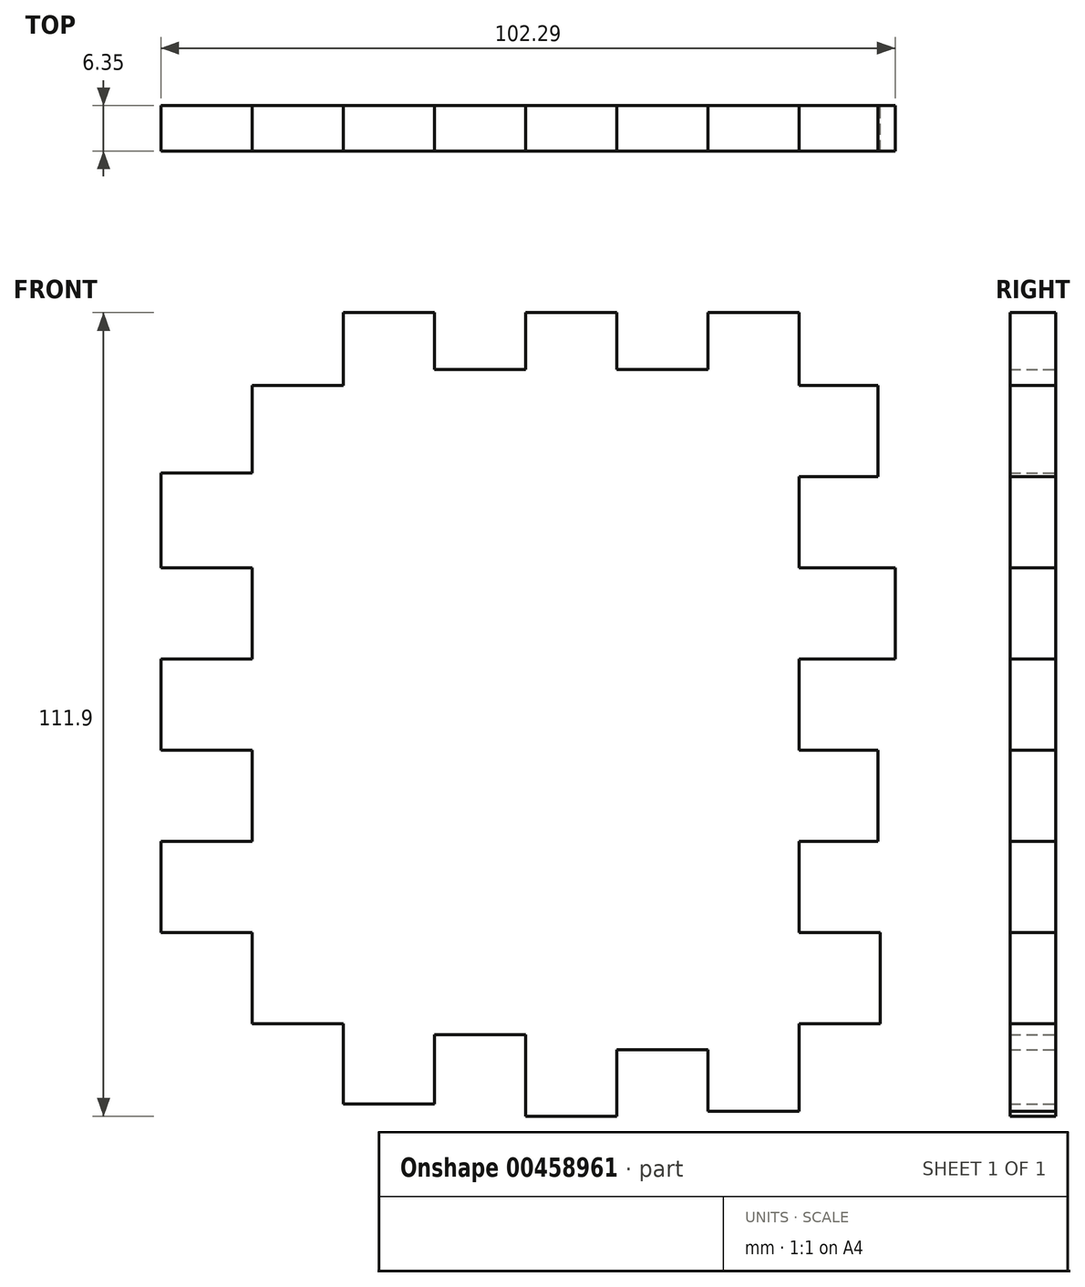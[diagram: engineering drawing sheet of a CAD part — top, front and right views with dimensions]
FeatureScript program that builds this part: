
annotation { "Feature Type Name" : "Feature", "Feature Type Description" : "" }
export const myFeature = defineFeature(function(context is Context, id is Id, definition is map)
    precondition{}
    {
        {
            var Q0;
            Q0=qCreatedBy(makeId("Front.planeOp"),FACE);
            var sketch = newSketch(context, id + "F0", { "sketchPlane" : qUnion([Q0])});
            skLineSegment(sketch, "E0", {"start": v(0, 35.53) * mm, "end": v(-12.7, 35.53) * mm});
            skLineSegment(sketch, "E1", {"start": v(-12.7, 35.53) * mm, "end": v(-12.7, 27.63) * mm});
            skLineSegment(sketch, "E2", {"start": v(-12.7, 27.63) * mm, "end": v(-25.4, 27.63) * mm});
            skLineSegment(sketch, "E3", {"start": v(-25.4, 27.63) * mm, "end": v(-25.4, 35.53) * mm});
            skLineSegment(sketch, "E4", {"start": v(-25.4, 35.53) * mm, "end": v(-38.1, 35.53) * mm});
            skLineSegment(sketch, "E5", {"start": v(-38.1, 35.53) * mm, "end": v(-38.1, 27.63) * mm});
            skLineSegment(sketch, "E6", {"start": v(-38.1, 27.63) * mm, "end": v(-50.8, 27.63) * mm});
            skLineSegment(sketch, "E7", {"start": v(-50.8, 27.63) * mm, "end": v(-50.8, 35.53) * mm});
            skLineSegment(sketch, "E8", {"start": v(-50.8, 35.53) * mm, "end": v(-63.5, 35.53) * mm});
            skLineSegment(sketch, "E9", {"start": v(-63.5, 35.53) * mm, "end": v(-63.5, 25.4) * mm});
            skLineSegment(sketch, "E10", {"start": v(-70.7, -63.5) * mm, "end": v(-63.5, -63.5) * mm});
            skLineSegment(sketch, "E11", {"start": v(-63.5, -63.5) * mm, "end": v(-63.5, -74.66) * mm});
            skLineSegment(sketch, "E12", {"start": v(-63.5, -74.66) * mm, "end": v(-50.8, -74.66) * mm});
            skLineSegment(sketch, "E13", {"start": v(-50.8, -74.66) * mm, "end": v(-50.8, -65.04) * mm});
            skLineSegment(sketch, "E14", {"start": v(-50.8, -65.04) * mm, "end": v(-38.1, -65.04) * mm});
            skLineSegment(sketch, "E15", {"start": v(-38.1, -65.04) * mm, "end": v(-38.1, -76.37) * mm});
            skLineSegment(sketch, "E16", {"start": v(-38.1, -76.37) * mm, "end": v(-25.4, -76.37) * mm});
            skLineSegment(sketch, "E17", {"start": v(-25.4, -76.37) * mm, "end": v(-25.4, -67.1) * mm});
            skLineSegment(sketch, "E18", {"start": v(0, 35.53) * mm, "end": v(0, 25.4) * mm});
            skLineSegment(sketch, "E19", {"start": v(0, 25.4) * mm, "end": v(10.98, 25.4) * mm});
            skLineSegment(sketch, "E20", {"start": v(10.98, 25.4) * mm, "end": v(10.98, 12.7) * mm});
            skLineSegment(sketch, "E21", {"start": v(10.98, 12.7) * mm, "end": v(0, 12.7) * mm});
            skLineSegment(sketch, "E22", {"start": v(0, 12.7) * mm, "end": v(0, 0) * mm});
            skLineSegment(sketch, "E23", {"start": v(0, 0) * mm, "end": v(13.39, 0) * mm});
            skLineSegment(sketch, "E24", {"start": v(13.39, 0) * mm, "end": v(13.39, -12.7) * mm});
            skLineSegment(sketch, "E25", {"start": v(13.39, -12.7) * mm, "end": v(0, -12.7) * mm});
            skLineSegment(sketch, "E26", {"start": v(0, -12.7) * mm, "end": v(0, -25.4) * mm});
            skLineSegment(sketch, "E27", {"start": v(0, -25.4) * mm, "end": v(10.98, -25.4) * mm});
            skLineSegment(sketch, "E28", {"start": v(10.98, -25.4) * mm, "end": v(10.98, -38.1) * mm});
            skLineSegment(sketch, "E29", {"start": v(10.98, -38.1) * mm, "end": v(0, -38.1) * mm});
            skLineSegment(sketch, "E30", {"start": v(0, -38.1) * mm, "end": v(0, -50.8) * mm});
            skLineSegment(sketch, "E31", {"start": v(0, -50.8) * mm, "end": v(11.33, -50.8) * mm});
            skLineSegment(sketch, "E32", {"start": v(11.33, -50.8) * mm, "end": v(11.33, -63.5) * mm});
            skLineSegment(sketch, "E33", {"start": v(11.33, -63.5) * mm, "end": v(0, -63.5) * mm});
            skLineSegment(sketch, "E34", {"start": v(0, -63.5) * mm, "end": v(0, -75.69) * mm});
            skLineSegment(sketch, "E35", {"start": v(0, -75.69) * mm, "end": v(-12.7, -75.69) * mm});
            skLineSegment(sketch, "E36", {"start": v(-25.4, -67.1) * mm, "end": v(-12.7, -67.1) * mm});
            skLineSegment(sketch, "E37", {"start": v(-12.7, -67.1) * mm, "end": v(-12.7, -75.69) * mm});
            skPoint(sketch, "E38.start.orphan", {"position": v(-70.7, 25.4) * mm});
            skPoint(sketch, "E39.start.orphan", {"position": v(-63.5, 12.7) * mm});
            skPoint(sketch, "E40.start.orphan", {"position": v(-63.5, 0) * mm});
            skPoint(sketch, "E41.start.orphan", {"position": v(-70.7, 0) * mm});
            skPoint(sketch, "E42.start.orphan", {"position": v(-63.5, -12.7) * mm});
            skPoint(sketch, "E43.start.orphan", {"position": v(-70.7, -25.4) * mm});
            skPoint(sketch, "E44.start.orphan", {"position": v(-63.5, -38.1) * mm});
            skPoint(sketch, "E45.start.orphan", {"position": v(-70.7, -50.8) * mm});
            skLineSegment(sketch, "E46", {"start": v(-63.5, 25.4) * mm, "end": v(-76.2, 25.4) * mm});
            skLineSegment(sketch, "E47", {"start": v(-76.2, 25.4) * mm, "end": v(-76.2, 13.18) * mm});
            skLineSegment(sketch, "E48", {"start": v(-76.2, 13.18) * mm, "end": v(-88.9, 13.18) * mm});
            skLineSegment(sketch, "E49", {"start": v(-88.9, 13.18) * mm, "end": v(-88.9, 0) * mm});
            skLineSegment(sketch, "E50", {"start": v(-88.9, 0) * mm, "end": v(-76.2, 0) * mm});
            skLineSegment(sketch, "E51", {"start": v(-76.2, 0) * mm, "end": v(-76.2, -12.7) * mm});
            skLineSegment(sketch, "E52", {"start": v(-76.2, -12.7) * mm, "end": v(-88.9, -12.7) * mm});
            skLineSegment(sketch, "E53", {"start": v(-88.9, -12.7) * mm, "end": v(-88.9, -25.4) * mm});
            skLineSegment(sketch, "E54", {"start": v(-88.9, -25.4) * mm, "end": v(-76.2, -25.4) * mm});
            skLineSegment(sketch, "E55", {"start": v(-76.2, -25.4) * mm, "end": v(-76.2, -38.1) * mm});
            skLineSegment(sketch, "E56", {"start": v(-76.2, -38.1) * mm, "end": v(-88.9, -38.1) * mm});
            skLineSegment(sketch, "E57", {"start": v(-88.9, -38.1) * mm, "end": v(-88.9, -50.8) * mm});
            skLineSegment(sketch, "E58", {"start": v(-88.9, -50.8) * mm, "end": v(-76.2, -50.8) * mm});
            skLineSegment(sketch, "E59", {"start": v(-76.2, -50.8) * mm, "end": v(-76.2, -63.5) * mm});
            skLineSegment(sketch, "E60", {"start": v(-76.2, -63.5) * mm, "end": v(-70.7, -63.5) * mm});
            skSolve(sketch);
        }
        {
            var Q0;
            Q0=makeQuery(id+"F0.imprint","IMPRINT",FACE,{"disambiguationData":[TD([[makeQuery(id+"F0.imprint","IMPRINT",EDGE,{"derivedFrom":sQuery(id+"F0.wireOp",EDGE,"E0")}),1.0]])]});
            extrude(context, id + "F1", {"entities" : qUnion([Q0]), "depth" : 6.35 * mm});
        }
    });
